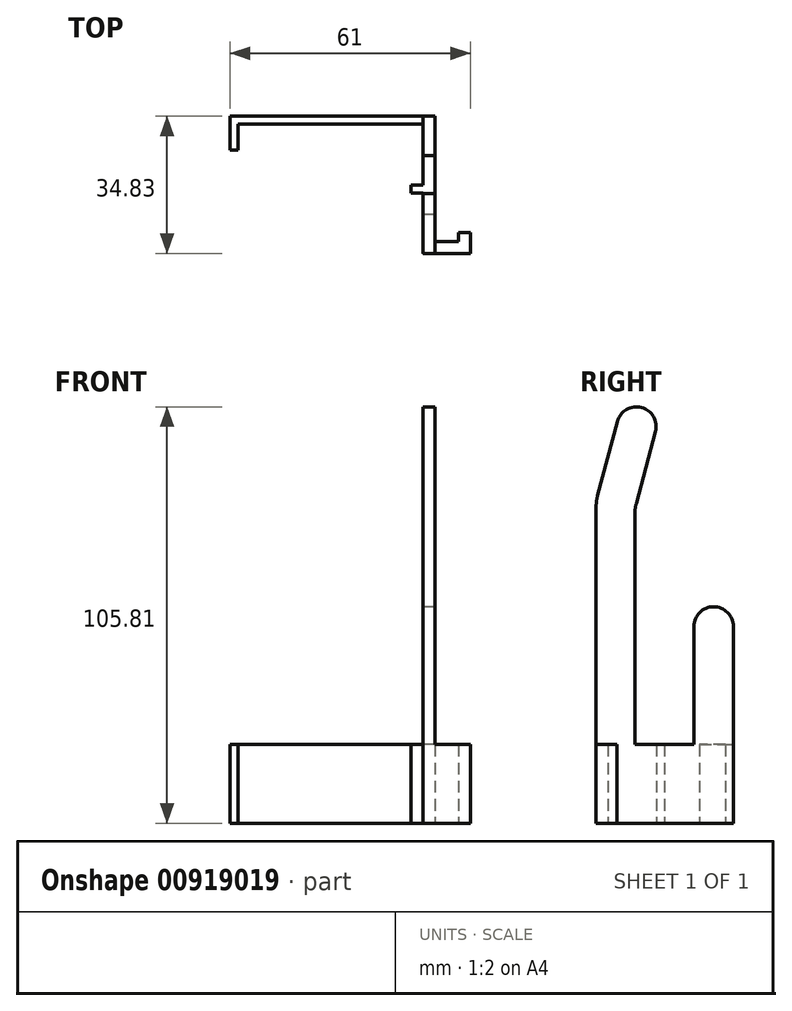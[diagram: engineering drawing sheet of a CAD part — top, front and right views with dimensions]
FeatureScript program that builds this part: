
annotation { "Feature Type Name" : "Feature", "Feature Type Description" : "" }
export const myFeature = defineFeature(function(context is Context, id is Id, definition is map)
    precondition{}
    {
        {
            var Q0;
            Q0=qCreatedBy(makeId("Top.planeOp"),FACE);
            var sketch = newSketch(context, id + "F0", { "sketchPlane" : qUnion([Q0])});
            skLineSegment(sketch, "E0.bottom", {"start": v(-28.87, 0) * mm, "end": v(29.81, 0) * mm});
            skLineSegment(sketch, "E1.top", {"start": v(-0.19, 15) * mm, "end": v(29.81, 15) * mm});
            skLineSegment(sketch, "E2.right", {"start": v(29.81, 15) * mm, "end": v(29.81, 0) * mm});
            skLineSegment(sketch, "E3.1", {"start": v(-30.82, -9.83) * mm, "end": v(49.81, -9.83) * mm});
            skLineSegment(sketch, "E3.2", {"start": v(49.81, 25) * mm, "end": v(49.81, -9.83) * mm});
            skLineSegment(sketch, "E3.3", {"start": v(-0.19, 25) * mm, "end": v(49.81, 25) * mm});
            skArc(sketch, "E4", {"start": v(-0.19, 25) * mm, "mid": v(-5.19, 20) * mm, "end": v(-0.19, 15) * mm});
            skLineSegment(sketch, "E5", {"start": v(-33.41, -9.49) * mm, "end": v(-52.3, -4.43) * mm});
            skLineSegment(sketch, "E6", {"start": v(-49.7, 5.23) * mm, "end": v(-31.46, 0.34) * mm});
            skArc(sketch, "E7", {"start": v(-49.7, 5.23) * mm, "mid": v(-55.83, 1.7) * mm, "end": v(-52.3, -4.43) * mm});
            skPoint(sketch, "E8.visualSharp", {"position": v(-30.19, 0) * mm});
            skArc(sketch, "E8.filletArc", {"start": v(-31.46, 0.34) * mm, "mid": v(-30.18, 0.09) * mm, "end": v(-28.87, 0) * mm});
            skPoint(sketch, "E9.visualSharp", {"position": v(-32.14, -9.83) * mm});
            skArc(sketch, "E9.filletArc", {"start": v(-33.41, -9.49) * mm, "mid": v(-32.13, -9.74) * mm, "end": v(-30.82, -9.83) * mm});
            skSolve(sketch);
        }
        {
            var Q0;
            Q0=makeQuery(id+"F0.imprint","IMPRINT",FACE,{"disambiguationData":[TD([[makeQuery(id+"F0.imprint","IMPRINT",EDGE,{"derivedFrom":sQuery(id+"F0.wireOp",EDGE,"E0.bottom")}),-1.0]])]});
            extrude(context, id + "F1", {"entities" : qUnion([Q0]), "depth" : 3 * mm, "offsetDistance" : 25 * mm});
        }
        {
            var Q0;
            Q0=makeQuery(id+"F1.opExtrude","SWEPT_FACE",FACE,{"disambiguationData":[OSD([sQuery(id+"F0.wireOp",EDGE,"E3.2")])]});
            var sketch = newSketch(context, id + "F2", { "sketchPlane" : qUnion([Q0])});
            skLineSegment(sketch, "E10", {"start": v(25, 0) * mm, "end": v(25, -49) * mm});
            skLineSegment(sketch, "E11", {"start": v(23, 0) * mm, "end": v(23, -47) * mm});
            skLineSegment(sketch, "E12", {"start": v(7.5, 0) * mm, "end": v(7.5, -3) * mm});
            skLineSegment(sketch, "E13", {"start": v(7.5, -3) * mm, "end": v(5.5, -3) * mm});
            skLineSegment(sketch, "E14", {"start": v(5.5, -3) * mm, "end": v(5.5, 0) * mm});
            skLineSegment(sketch, "E15", {"start": v(25, -49) * mm, "end": v(16.38, -49) * mm});
            skLineSegment(sketch, "E16", {"start": v(16.38, -49) * mm, "end": v(16.38, -47) * mm});
            skLineSegment(sketch, "E17", {"start": v(16.38, -47) * mm, "end": v(23, -47) * mm});
            skLineSegment(sketch, "E18", {"start": v(-9.83, 3) * mm, "end": v(-9.83, 12) * mm});
            skLineSegment(sketch, "E19", {"start": v(-9.83, 12) * mm, "end": v(-4.5, 12) * mm});
            skLineSegment(sketch, "E20", {"start": v(-4.5, 12) * mm, "end": v(-4.5, 9) * mm});
            skLineSegment(sketch, "E21", {"start": v(-4.5, 9) * mm, "end": v(-6.83, 9) * mm});
            skLineSegment(sketch, "E22", {"start": v(-6.83, 9) * mm, "end": v(-6.83, 3) * mm});
            skSolve(sketch);
        }
        {
            var Q0;
            {var subQ1=sQuery(id+"F2.wireOp",EDGE,"E10");Q0=makeQuery(id+"F2.imprint","IMPRINT",FACE,{"disambiguationData":[TD([[makeQuery(id+"F2.imprint","IMPRINT",EDGE,{"derivedFrom":subQ1}),-1.0]])]});}
            var Q1;
            {var subQ0=sQuery(id+"F2.wireOp",EDGE,"E12");Q1=makeQuery(id+"F2.imprint","IMPRINT",FACE,{"disambiguationData":[TD([[makeQuery(id+"F2.imprint","IMPRINT",EDGE,{"derivedFrom":subQ0}),-1.0]])]});}
            var Q2;
            {var subQ0=sQuery(id+"F2.wireOp",EDGE,"E18");Q2=makeQuery(id+"F2.imprint","IMPRINT",FACE,{"disambiguationData":[TD([[makeQuery(id+"F2.imprint","IMPRINT",EDGE,{"derivedFrom":subQ0}),-1.0]])]});}
            var Q3;
            Q3=makeQuery(id+"F1.opExtrude","SWEPT_FACE",FACE,{"disambiguationData":[OSD([sQuery(id+"F0.wireOp",EDGE,"E2.right")])]});
            extrude(context, id + "F3", {"entities" : qUnion([Q0, Q1, Q2]), "operationType" : NewBodyOperationType.ADD, "endBound" : BoundingType.UP_TO_SURFACE, "oppositeDirection" : true, "depth" : 25 * mm, "endBoundEntityFace" : qUnion([Q3]), "offsetDistance" : 25 * mm});
        }
        {
            var Q0;
            Q0=makeQuery(id+"F1.opExtrude","SWEPT_BODY",BODY,{"disambiguationData":[OSD([sQuery(id+"F0.wireOp",EDGE,"E0.bottom"),sQuery(id+"F0.wireOp",EDGE,"E1.top"),sQuery(id+"F0.wireOp",EDGE,"E2.right"),sQuery(id+"F0.wireOp",EDGE,"E3.1"),sQuery(id+"F0.wireOp",EDGE,"E3.2"),sQuery(id+"F0.wireOp",EDGE,"E3.3"),sQuery(id+"F0.wireOp",EDGE,"E4"),sQuery(id+"F0.wireOp",EDGE,"E5"),sQuery(id+"F0.wireOp",EDGE,"E6"),sQuery(id+"F0.wireOp",EDGE,"E7")])]});
            var Q1;
            Q1=makeQuery(id+"F1.opExtrude","CAP_EDGE",EDGE,{"disambiguationData":[OSD([sQuery(id+"F0.wireOp",EDGE,"E3.2")])],"isStart":false});
            transform(context, id + "F4", {"entities" : qUnion([Q0]), "transformType" : TransformType.ROTATION, "transformAxis" : qUnion([Q1]), "angle" : 90 * degree, "oppositeDirection" : true, "makeCopy" : false});
        }
    });
